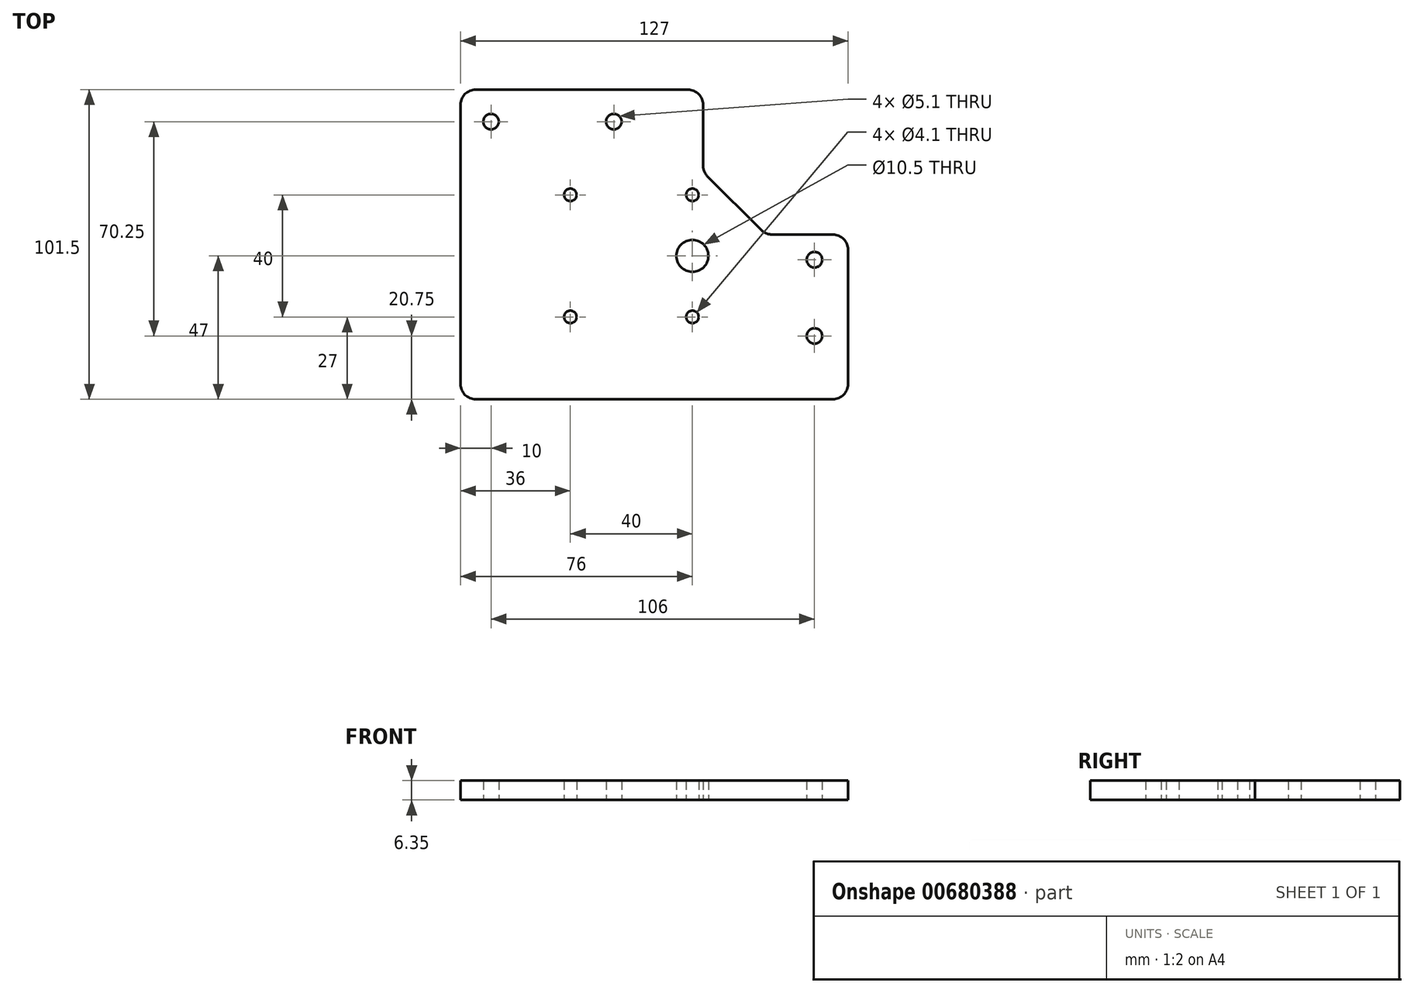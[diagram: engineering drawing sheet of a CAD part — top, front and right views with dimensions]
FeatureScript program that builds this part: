
annotation { "Feature Type Name" : "Feature", "Feature Type Description" : "" }
export const myFeature = defineFeature(function(context is Context, id is Id, definition is map)
    precondition{}
    {
        {
            var Q0;
            Q0=qCreatedBy(makeId("Top.planeOp"),FACE);
            var sketch = newSketch(context, id + "F0", { "sketchPlane" : qUnion([Q0])});
            skLineSegment(sketch, "E0", {"start": v(0, 0) * mm, "end": v(127, 0) * mm});
            skLineSegment(sketch, "E1", {"start": v(0, 0) * mm, "end": v(0, 101.5) * mm});
            skLineSegment(sketch, "E2", {"start": v(0, 101.5) * mm, "end": v(79.5, 101.5) * mm});
            skLineSegment(sketch, "E3", {"start": v(127, 0) * mm, "end": v(127, 54) * mm});
            skLineSegment(sketch, "E4", {"start": v(79.5, 101.5) * mm, "end": v(79.5, 74.5) * mm});
            skLineSegment(sketch, "E5", {"start": v(127, 54) * mm, "end": v(100, 54) * mm});
            skLineSegment(sketch, "E6", {"start": v(79.5, 74.5) * mm, "end": v(100, 54) * mm});
            skCircle(sketch, "E7", {"center": v(10, 91) * mm, "radius": 2.55 * mm});
            skCircle(sketch, "E8", {"center": v(50.25, 91) * mm, "radius": 2.55 * mm});
            skCircle(sketch, "E9", {"center": v(116, 45.75) * mm, "radius": 2.55 * mm});
            skCircle(sketch, "E10", {"center": v(116, 20.75) * mm, "radius": 2.55 * mm});
            skCircle(sketch, "E11", {"center": v(36, 67) * mm, "radius": 2.05 * mm});
            skCircle(sketch, "E12", {"center": v(76, 67) * mm, "radius": 2.05 * mm});
            skCircle(sketch, "E13", {"center": v(36, 27) * mm, "radius": 2.05 * mm});
            skCircle(sketch, "E14", {"center": v(76, 27) * mm, "radius": 2.05 * mm});
            skLineSegment(sketch, "E15.bottom", {"start": v(36, 67) * mm, "end": v(76, 67) * mm});
            skLineSegment(sketch, "E15.top", {"start": v(36, 27) * mm, "end": v(76, 27) * mm});
            skLineSegment(sketch, "E15.left", {"start": v(36, 67) * mm, "end": v(36, 27) * mm});
            skLineSegment(sketch, "E15.right", {"start": v(76, 67) * mm, "end": v(76, 27) * mm});
            skCircle(sketch, "E16", {"center": v(76, 47) * mm, "radius": 5.25 * mm});
            skSolve(sketch);
        }
        {
            var Q0;
            Q0=makeQuery(id+"F0.imprint","IMPRINT",FACE,{"disambiguationData":[TD([[makeQuery(id+"F0.imprint","IMPRINT",EDGE,{"derivedFrom":sQuery(id+"F0.wireOp",EDGE,"E0")}),1.0]])]});
            var Q1;
            {var subQ5=sQuery(id+"F0.wireOp",EDGE,"E11");var subQ7=sQuery(id+"F0.wireOp",EDGE,"E15.bottom");var subQ15=makeQuery(id+"F0.imprint","INTERSECT",VERTEX,{"derivedFrom":[subQ5,subQ7]});Q1=makeQuery(id+"F0.imprint","IMPRINT",FACE,{"disambiguationData":[TD([[makeQuery(id+"F0.imprint","IMPRINT",EDGE,{"disambiguationData":[TD([[subQ15,1.0]])],"derivedFrom":subQ5}),-1.0]])]});}
            extrude(context, id + "F1", {"entities" : qUnion([Q0, Q1]), "depth" : 6.35 * mm, "offsetDistance" : 25 * mm});
        }
        {
            var Q0;
            Q0=makeQuery(id+"F1.opExtrude","SWEPT_EDGE",EDGE,{"disambiguationData":[OSD([sQuery(id+"F0.wireOp",EDGE,"E4"),sQuery(id+"F0.wireOp",EDGE,"E6")])]});
            var Q1;
            Q1=makeQuery(id+"F1.opExtrude","SWEPT_EDGE",EDGE,{"disambiguationData":[OSD([sQuery(id+"F0.wireOp",EDGE,"E5"),sQuery(id+"F0.wireOp",EDGE,"E6")])]});
            fillet(context, id + "F2", {"entities" : qUnion([Q0, Q1]), "radius" : 5 * mm, "tangentPropagation" : true, "allowEdgeOverflow" : false});
        }
        {
            var Q0;
            Q0=makeQuery(id+"F1.opExtrude","SWEPT_EDGE",EDGE,{"disambiguationData":[OSD([sQuery(id+"F0.wireOp",EDGE,"E1"),sQuery(id+"F0.wireOp",EDGE,"E2")])]});
            var Q1;
            Q1=makeQuery(id+"F1.opExtrude","SWEPT_EDGE",EDGE,{"disambiguationData":[OSD([sQuery(id+"F0.wireOp",EDGE,"E2"),sQuery(id+"F0.wireOp",EDGE,"E4")])]});
            var Q2;
            Q2=makeQuery(id+"F1.opExtrude","SWEPT_EDGE",EDGE,{"disambiguationData":[OSD([sQuery(id+"F0.wireOp",EDGE,"E3"),sQuery(id+"F0.wireOp",EDGE,"E5")])]});
            var Q3;
            Q3=makeQuery(id+"F1.opExtrude","SWEPT_EDGE",EDGE,{"disambiguationData":[OSD([sQuery(id+"F0.wireOp",EDGE,"E0"),sQuery(id+"F0.wireOp",EDGE,"E3")])]});
            var Q4;
            Q4=makeQuery(id+"F1.opExtrude","SWEPT_EDGE",EDGE,{"disambiguationData":[OSD([sQuery(id+"F0.wireOp",EDGE,"E0"),sQuery(id+"F0.wireOp",EDGE,"E1")])]});
            fillet(context, id + "F3", {"entities" : qUnion([Q0, Q1, Q2, Q3, Q4]), "radius" : 5 * mm, "tangentPropagation" : true, "allowEdgeOverflow" : false});
        }
    });
